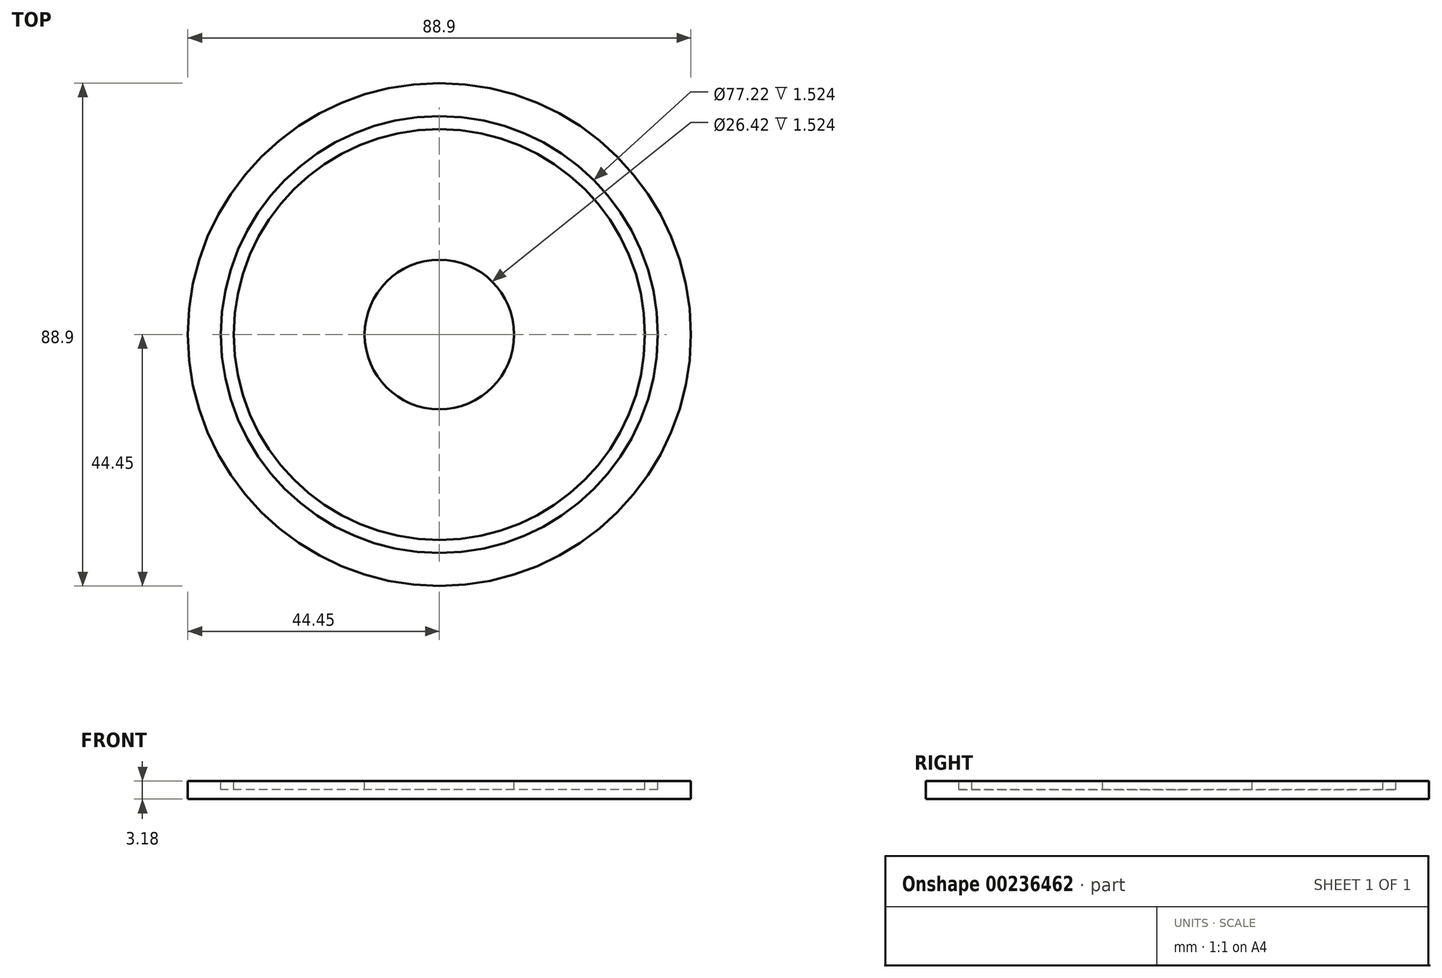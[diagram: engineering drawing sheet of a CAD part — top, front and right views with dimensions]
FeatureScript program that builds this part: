
annotation { "Feature Type Name" : "Feature", "Feature Type Description" : "" }
export const myFeature = defineFeature(function(context is Context, id is Id, definition is map)
    precondition{}
    {
        {
            var Q0;
            Q0=qCreatedBy(makeId("Top.planeOp"),FACE);
            var sketch = newSketch(context, id + "F0", { "sketchPlane" : qUnion([Q0])});
            skCircle(sketch, "E0", {"center": v(0, 0) * mm, "radius": 44.45 * mm});
            skSolve(sketch);
        }
        {
            var Q0;
            Q0 = qSketchRegion(id + "F0", true);
            extrude(context, id + "F1", {"entities" : qUnion([Q0]), "depth" : 3.17 * mm});
        }
        {
            var Q0;
            Q0=makeQuery(id+"F1.opExtrude","CAP_FACE",FACE,{"disambiguationData":[OSD([sQuery(id+"F0.wireOp",EDGE,"E0")])],"isStart":false});
            var sketch = newSketch(context, id + "F2", { "sketchPlane" : qUnion([Q0])});
            skCircle(sketch, "E1", {"center": v(0, 0) * mm, "radius": 38.6 * mm});
            skCircle(sketch, "E2", {"center": v(0, 0) * mm, "radius": 36.32 * mm});
            skCircle(sketch, "E3", {"center": v(0, 0) * mm, "radius": 13.2 * mm});
            skSolve(sketch);
        }
        {
            var Q0;
            Q0 = qSketchRegion(id + "F2", true);
            var Q1;
            Q1=makeQuery(id+"F2.imprint","IMPRINT",FACE,{"disambiguationData":[TD([[makeQuery(id+"F2.imprint","IMPRINT",EDGE,{"derivedFrom":sQuery(id+"F2.wireOp",EDGE,"E3")}),1.0]])]});
            extrude(context, id + "F3", {"entities" : qUnion([Q0, Q1]), "operationType" : NewBodyOperationType.REMOVE, "oppositeDirection" : true, "depth" : 1.52 * mm});
        }
    });
